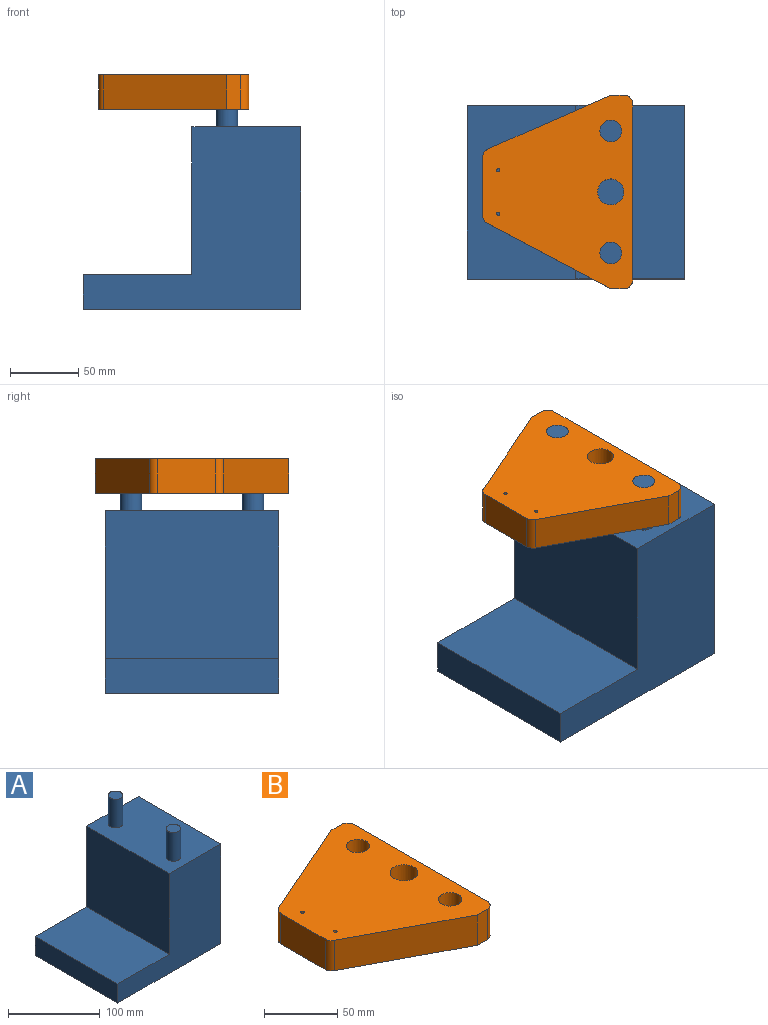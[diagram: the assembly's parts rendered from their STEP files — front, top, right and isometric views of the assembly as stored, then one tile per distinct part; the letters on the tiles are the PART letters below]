
ASSEMBLY  parts=2 mates=1
PART A: 12 faces, bbox 158.8x127x171.5 mm
  f0: plane 133.35x127mm, normal (1,0,0), area 16935.5mm2, adj f1,f3,f5,f7
  f1: plane 158.75x133.35mm, normal (0,1,0), area 12602.2mm2, adj f0,f2,f4,f5,f6,f7
  f2: plane 127x25.4mm, normal (-1,0,0), area 3225.8mm2, adj f1,f3,f4,f5
  f3: plane 158.75x133.35mm, normal (0,-1,0), area 12602.2mm2, adj f0,f2,f4,f5,f6,f7
  f4: plane 127x79.36mm, normal (0,0,1), area 10079mm2, adj f1,f2,f3,f6
  f5: plane 158.75x127mm, normal (0,0,-1), area 20161.3mm2, adj f0,f1,f2,f3
  f6: plane 127x107.95mm, normal (-1,0,0), area 13709.6mm2, adj f1,f3,f4,f7
  f7: plane 127x79.39mm, normal (0,0,1), area 9686.4mm2, adj f0,f1,f3,f6,f8,f10
  f8: cylinder r=7.94mm len=38.1mm, axis (0,0,-1), area 1900.2mm2, adj f7,f9
  f9: plane 15.88x15.88mm, normal (0,0,1), area 197.9mm2, adj f8
  f10: cylinder r=7.94mm len=38.1mm, axis (0,0,-1), area 1900.2mm2, adj f7,f11
  f11: plane 15.88x15.88mm, normal (0,0,1), area 197.9mm2, adj f10
PART B: 17 faces, bbox 109.8x141.3x25.4 mm
  f0: plane 89.85x39.28mm, normal (-0.4,0.92,0), area 2490.7mm2, adj f1,f14,f15,f16
  f1: cylinder r=6.35mm len=25.4mm, axis (0,0,1), area 186.9mm2, adj f0,f2,f15,f16
  f2: plane 42.82x25.4mm, normal (-1,0,0), area 1087.6mm2, adj f1,f3,f15,f16
  f3: cylinder r=6.35mm len=25.4mm, axis (0,0,1), area 174.9mm2, adj f2,f4,f15,f16
  f4: plane 90.28x47.75mm, normal (-0.47,-0.88,0), area 2593.9mm2, adj f3,f5,f15,f16
  f5: plane 25.4x9.78mm, normal (0,-1,0), area 248.4mm2, adj f4,f6,f15,f16
  f6: cylinder r=6.35mm len=25.4mm, axis (0,0,1), area 253.4mm2, adj f5,f7,f15,f16
  f7: plane 128.57x25.4mm, normal (1,0,0), area 3265.8mm2, adj f6,f8,f15,f16
  f8: cylinder r=6.35mm len=25.4mm, axis (0,0,1), area 253.4mm2, adj f7,f14,f15,f16
  f9: cylinder r=7.94mm len=25.4mm, axis (0,0,1), area 1266.8mm2, adj f15,f16
  f10: cylinder r=7.94mm len=25.4mm, axis (0,0,1), area 1266.8mm2, adj f15,f16
  f11: cylinder r=1.19mm len=25.4mm, axis (0,0,1), area 189.9mm2, adj f15,f16
  f12: cylinder r=1.19mm len=25.4mm, axis (0,0,1), area 189.9mm2, adj f15,f16
  f13: cylinder r=9.53mm len=25.4mm, axis (0,0,1), area 1520.1mm2, adj f15,f16
  f14: plane 25.4x9.78mm, normal (0,1,0), area 248.4mm2, adj f0,f8,f15,f16
  f15: plane 141.28x109.79mm, normal (0,0,-1), area 10560.6mm2, adj f0,f1,f2,f3,f4,f5,f6,f7
  f16: plane 141.28x109.79mm, normal (0,0,1), area 10560.6mm2, adj f0,f1,f2,f3,f4,f5,f6,f7
PLACE A at identity
PLACE B t=(120.89,63.5,171.45)mm
MATE slider B.f10 <-> A.f10  axis (0,0,-1) through (104.76,18.94,146.05)mm
